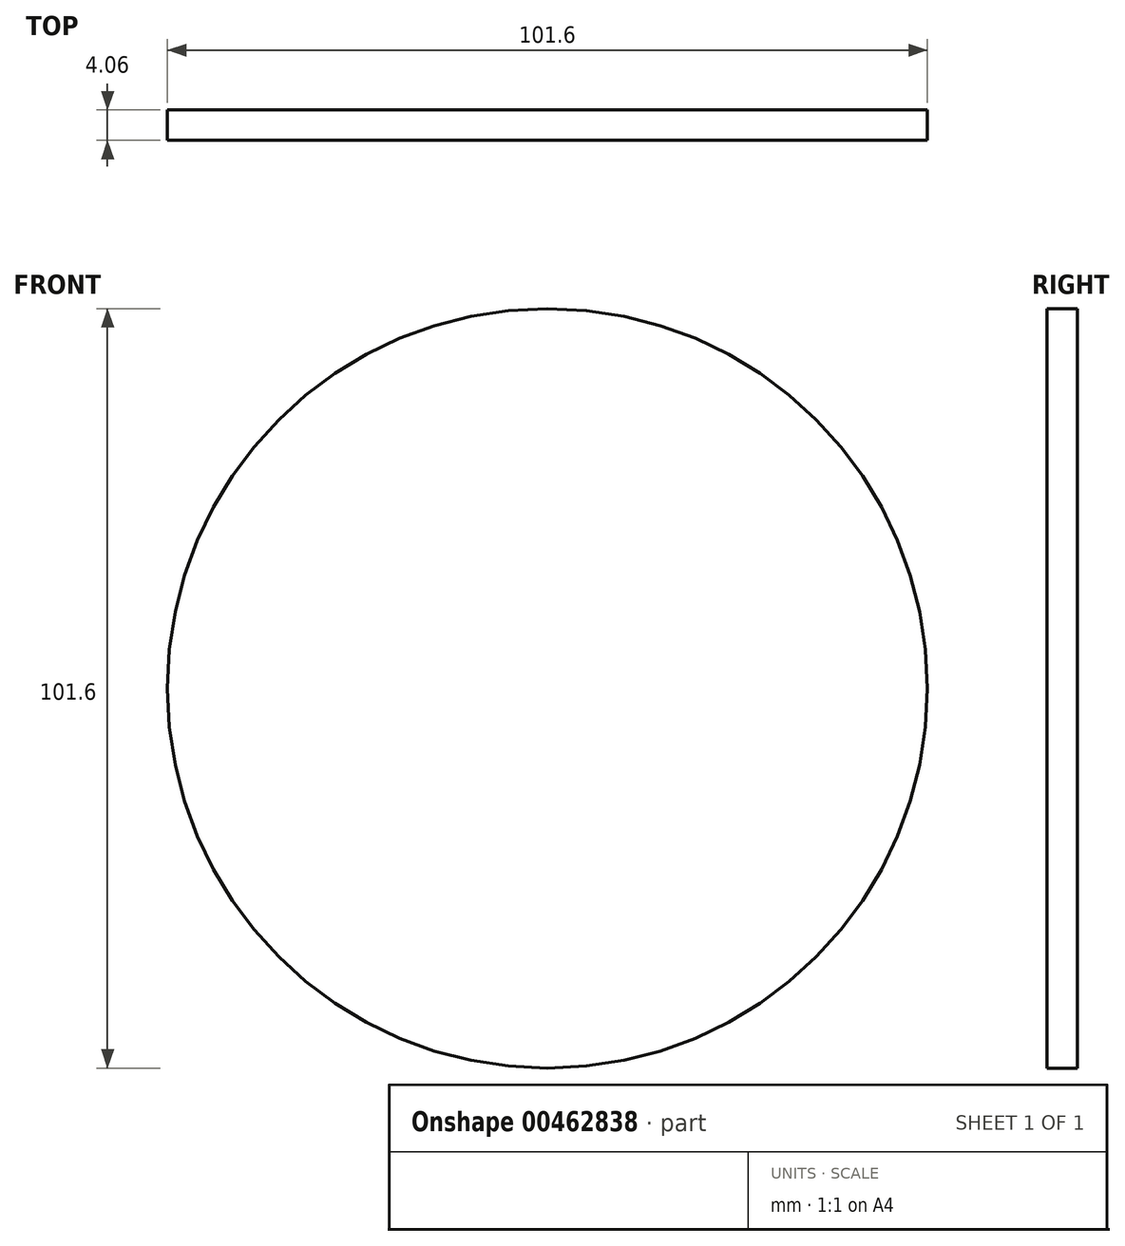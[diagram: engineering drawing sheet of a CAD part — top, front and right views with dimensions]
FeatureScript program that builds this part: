
annotation { "Feature Type Name" : "Feature", "Feature Type Description" : "" }
export const myFeature = defineFeature(function(context is Context, id is Id, definition is map)
    precondition{}
    {
        {
            var Q0;
            Q0=qCreatedBy(makeId("Front.planeOp"),FACE);
            var sketch = newSketch(context, id + "F0", { "sketchPlane" : qUnion([Q0])});
            skCircle(sketch, "E0", {"center": v(0, 0) * mm, "radius": 50.8 * mm});
            skSolve(sketch);
        }
        {
            var Q0;
            Q0=makeQuery(id+"F0.imprint","IMPRINT",FACE,{"disambiguationData":[TD([[makeQuery(id+"F0.imprint","IMPRINT",EDGE,{"derivedFrom":sQuery(id+"F0.wireOp",EDGE,"E0")}),1.0]])]});
            extrude(context, id + "F1", {"entities" : qUnion([Q0]), "depth" : 4.06 * mm});
        }
    });
